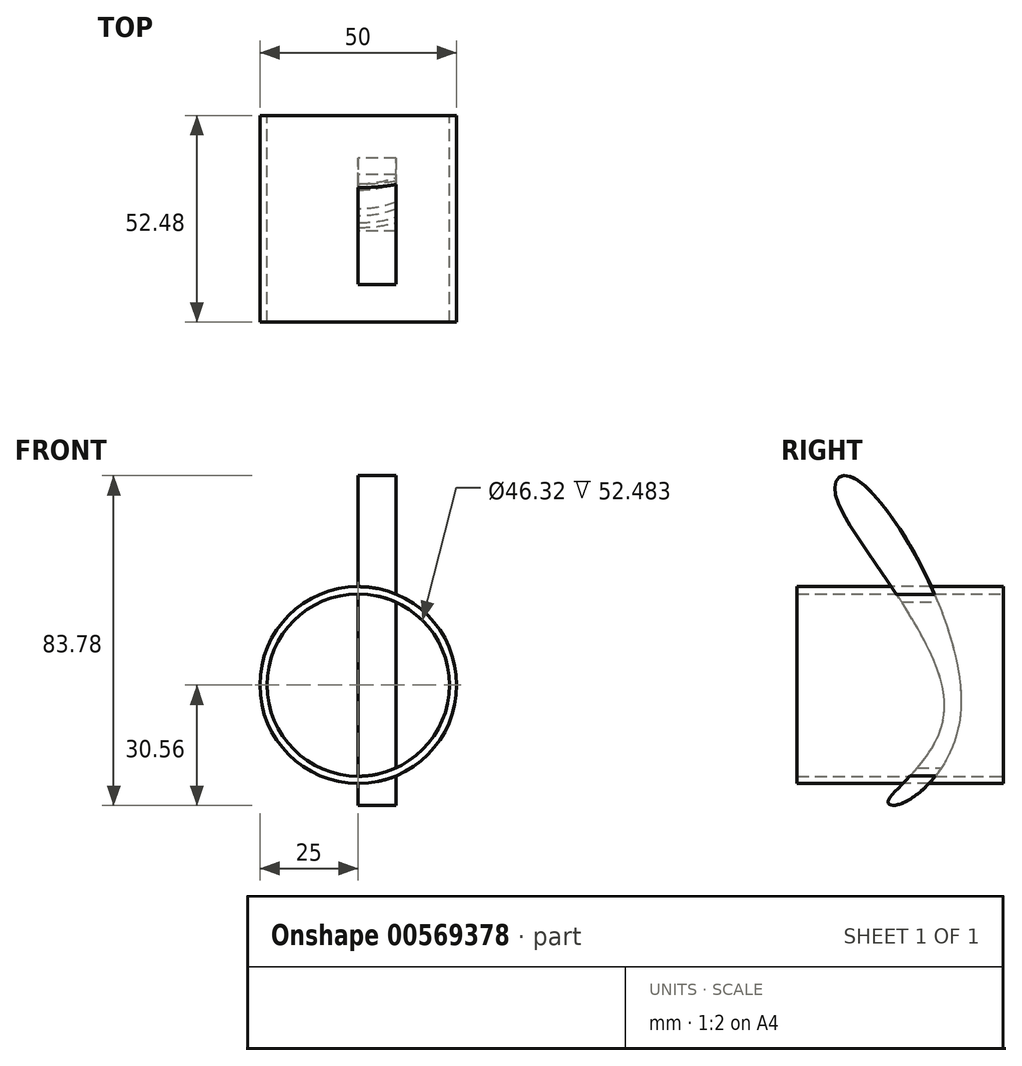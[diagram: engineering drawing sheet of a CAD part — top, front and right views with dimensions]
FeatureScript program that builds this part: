
annotation { "Feature Type Name" : "Feature", "Feature Type Description" : "" }
export const myFeature = defineFeature(function(context is Context, id is Id, definition is map)
    precondition{}
    {
        {
            var Q0;
            Q0=qCreatedBy(makeId("Front.planeOp"),FACE);
            var sketch = newSketch(context, id + "F0", { "sketchPlane" : qUnion([Q0])});
            skCircle(sketch, "E0", {"center": v(0, 0) * mm, "radius": 25 * mm});
            skSolve(sketch);
        }
        {
            var Q0;
            Q0 = qSketchRegion(id + "F0", true);
            extrude(context, id + "F1", {"entities" : qUnion([Q0]), "oppositeDirection" : true, "depth" : 52.48 * mm, "offsetDistance" : 25 * mm});
        }
        {
            var Q0;
            Q0=makeQuery(id+"F1.opExtrude","CAP_FACE",FACE,{"disambiguationData":[OSD([sQuery(id+"F0.wireOp",EDGE,"E0")])],"isStart":false});
            var sketch = newSketch(context, id + "F2", { "sketchPlane" : qUnion([Q0])});
            skCircle(sketch, "E1", {"center": v(0, 0) * mm, "radius": 45 * mm});
            skSolve(sketch);
        }
        {
            var Q0;
            Q0=sQuery(id+"F2.wireOp",EDGE,"E1");
            var Q1;
            Q1=makeQuery(id+"F1.opExtrude","CAP_FACE",FACE,{"disambiguationData":[OSD([sQuery(id+"F0.wireOp",EDGE,"E0")])],"isStart":true});
            loft(context, id + "F3", {"bodyType" : ToolBodyType.SURFACE, "wireProfilesArray" : [{ "wireProfileEntities" : qUnion([Q0]) }, { "wireProfileEntities" : qUnion([Q1]) }]});
        }
        {
            var Q0;
            Q0=makeQuery(id+"F1.opExtrude","CAP_FACE",FACE,{"disambiguationData":[OSD([sQuery(id+"F0.wireOp",EDGE,"E0")])],"isStart":false});
            var sketch = newSketch(context, id + "F4", { "sketchPlane" : qUnion([Q0])});
            skCircle(sketch, "E2", {"center": v(0, 0) * mm, "radius": 23.16 * mm});
            skSolve(sketch);
        }
        {
            var Q0;
            Q0 = qSketchRegion(id + "F4", true);
            extrude(context, id + "F5", {"entities" : qUnion([Q0]), "operationType" : NewBodyOperationType.REMOVE, "oppositeDirection" : true, "depth" : 56.22 * mm, "offsetDistance" : 25 * mm});
        }
        {
            var Q0;
            Q0=qCreatedBy(makeId("Right.planeOp"),FACE);
            var sketch = newSketch(context, id + "F6", { "sketchPlane" : qUnion([Q0])});
            skFitSpline(sketch, "E3", {"points": [v(13.57, 52.98) * mm, v(41.63, -6.43) * mm, v(25.2, -30.5) * mm, v(23.19, -29.51) * mm, v(37.5, -6.43) * mm, v(9.71, 48.9) * mm, v(13.57, 52.98) * mm]});
            skSolve(sketch);
        }
        {
            var Q0;
            Q0 = qSketchRegion(id + "F6", true);
            extrude(context, id + "F7", {"entities" : qUnion([Q0]), "operationType" : NewBodyOperationType.ADD, "depth" : 9.6 * mm, "offsetDistance" : 25 * mm});
        }
    });
